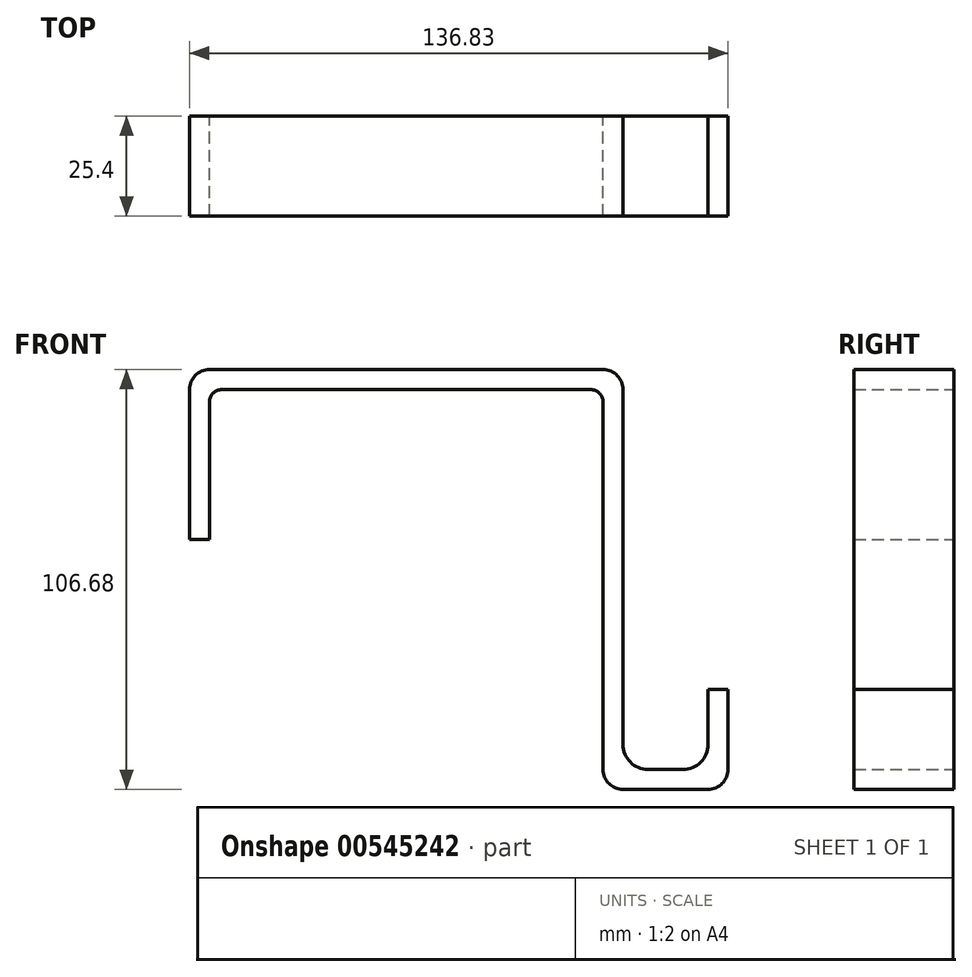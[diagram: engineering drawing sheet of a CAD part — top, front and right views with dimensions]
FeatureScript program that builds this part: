
annotation { "Feature Type Name" : "Feature", "Feature Type Description" : "" }
export const myFeature = defineFeature(function(context is Context, id is Id, definition is map)
    precondition{}
    {
        {
            var Q0;
            Q0=qCreatedBy(makeId("Front.planeOp"),FACE);
            var sketch = newSketch(context, id + "F0", { "sketchPlane" : qUnion([Q0])});
            skLineSegment(sketch, "E0", {"start": v(0, 0) * mm, "end": v(0, 43.18) * mm});
            skLineSegment(sketch, "E1", {"start": v(0, 43.18) * mm, "end": v(110.16, 43.18) * mm});
            skLineSegment(sketch, "E2", {"start": v(110.16, 43.18) * mm, "end": v(110.16, -52.07) * mm});
            skLineSegment(sketch, "E3", {"start": v(116.51, -58.42) * mm, "end": v(125.4, -58.42) * mm});
            skLineSegment(sketch, "E4", {"start": v(131.75, -52.07) * mm, "end": v(131.75, -38.1) * mm});
            skLineSegment(sketch, "E5.0", {"start": v(136.83, -63.5) * mm, "end": v(136.83, -38.1) * mm});
            skLineSegment(sketch, "E5.1", {"start": v(5.08, 0) * mm, "end": v(5.08, 34.93) * mm});
            skLineSegment(sketch, "E5.2", {"start": v(8.25, 38.1) * mm, "end": v(101.9, 38.1) * mm});
            skLineSegment(sketch, "E5.3", {"start": v(105.08, 34.93) * mm, "end": v(105.08, -63.5) * mm});
            skLineSegment(sketch, "E5.4", {"start": v(105.08, -63.5) * mm, "end": v(136.83, -63.5) * mm});
            skLineSegment(sketch, "E6", {"start": v(5.08, 0) * mm, "end": v(0, 0) * mm});
            skLineSegment(sketch, "E7", {"start": v(131.75, -38.1) * mm, "end": v(136.83, -38.1) * mm});
            skPoint(sketch, "E8.visualSharp", {"position": v(110.16, -58.42) * mm});
            skArc(sketch, "E8.filletArc", {"start": v(110.16, -52.07) * mm, "mid": v(112.02, -56.56) * mm, "end": v(116.51, -58.42) * mm});
            skPoint(sketch, "E9.visualSharp", {"position": v(131.75, -58.42) * mm});
            skArc(sketch, "E9.filletArc", {"start": v(125.4, -58.42) * mm, "mid": v(129.9, -56.56) * mm, "end": v(131.75, -52.07) * mm});
            skPoint(sketch, "E10.visualSharp", {"position": v(5.08, 38.1) * mm});
            skPoint(sketch, "E11.visualSharp", {"position": v(105.08, 38.1) * mm});
            skArc(sketch, "E12.filletArc", {"start": v(8.25, 38.1) * mm, "mid": v(6, 37.17) * mm, "end": v(5.08, 34.93) * mm});
            skArc(sketch, "E13.filletArc", {"start": v(105.08, 34.93) * mm, "mid": v(104.15, 37.17) * mm, "end": v(101.9, 38.1) * mm});
            skSolve(sketch);
        }
        {
            var Q0;
            Q0=qSketchRegion(id+"F0",true);
            extrude(context, id + "F1", {"entities" : qUnion([Q0]), "depth" : 25.4 * mm});
        }
        {
            var Q0;
            Q0=makeQuery(id+"F1.opExtrude","SWEPT_EDGE",EDGE,{"disambiguationData":[OSD([sQuery(id+"F0.wireOp",EDGE,"E0"),sQuery(id+"F0.wireOp",EDGE,"E1")])]});
            var Q1;
            Q1=makeQuery(id+"F1.opExtrude","SWEPT_EDGE",EDGE,{"disambiguationData":[OSD([sQuery(id+"F0.wireOp",EDGE,"E1"),sQuery(id+"F0.wireOp",EDGE,"E2")])]});
            var Q2;
            Q2=makeQuery(id+"F1.opExtrude","SWEPT_EDGE",EDGE,{"disambiguationData":[OSD([sQuery(id+"F0.wireOp",EDGE,"E5.0"),sQuery(id+"F0.wireOp",EDGE,"E5.4")])]});
            var Q3;
            Q3=makeQuery(id+"F1.opExtrude","SWEPT_EDGE",EDGE,{"disambiguationData":[OSD([sQuery(id+"F0.wireOp",EDGE,"E5.3"),sQuery(id+"F0.wireOp",EDGE,"E5.4")])]});
            fillet(context, id + "F2", {"entities" : qUnion([Q0, Q1, Q2, Q3]), "radius" : 5.08 * mm, "tangentPropagation" : true, "allowEdgeOverflow" : false});
        }
    });
